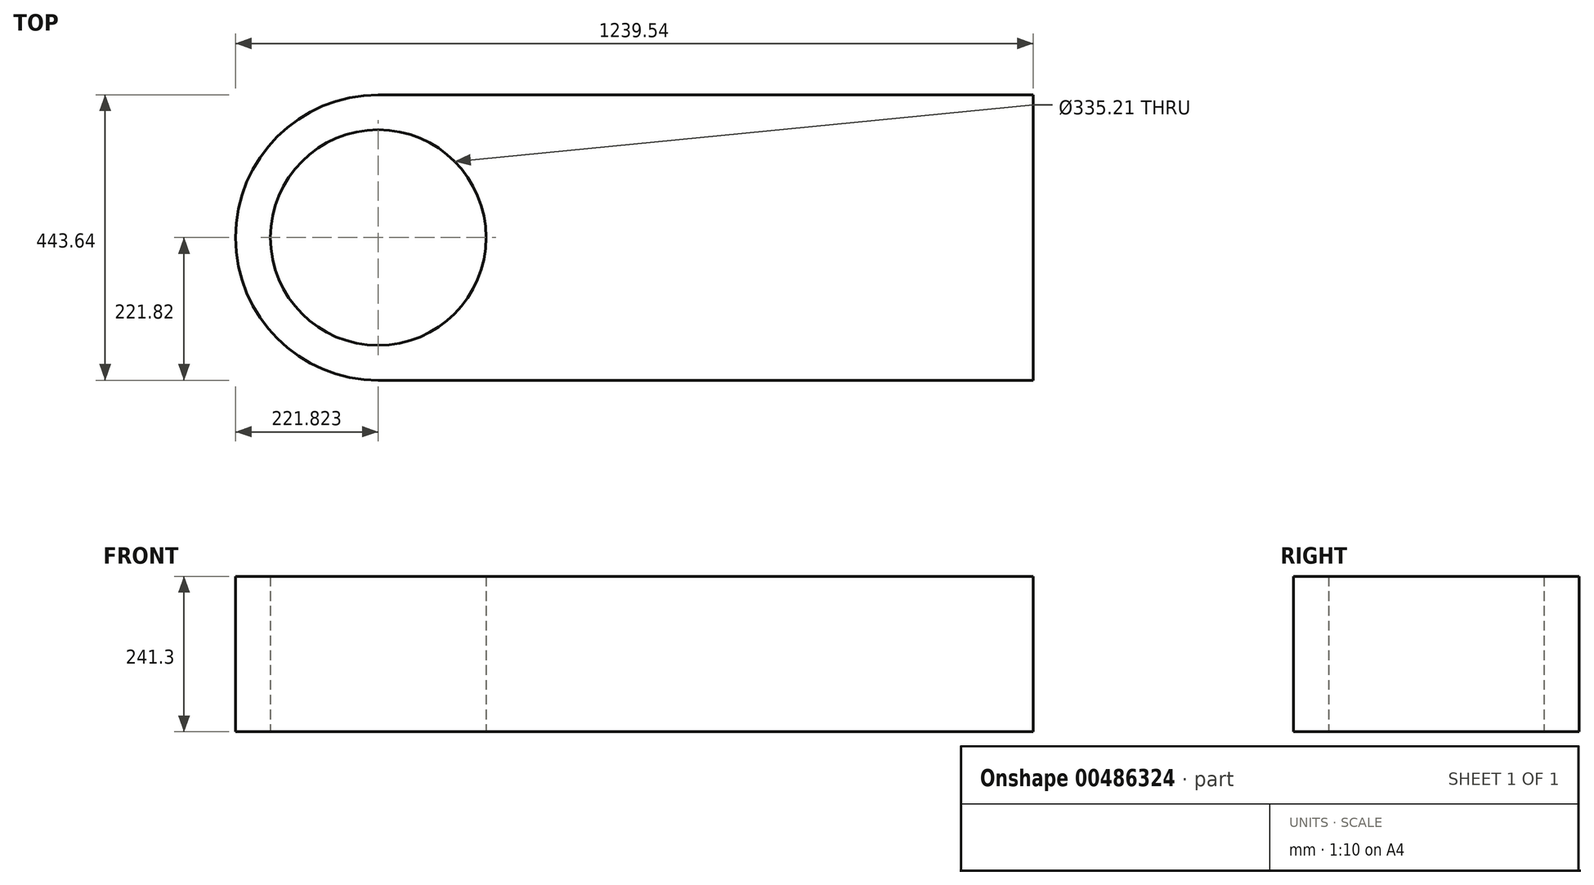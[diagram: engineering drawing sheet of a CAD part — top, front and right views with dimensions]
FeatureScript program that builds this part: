
annotation { "Feature Type Name" : "Feature", "Feature Type Description" : "" }
export const myFeature = defineFeature(function(context is Context, id is Id, definition is map)
    precondition{}
    {
        {
            var Q0;
            Q0=qCreatedBy(makeId("Top.planeOp"),FACE);
            var sketch = newSketch(context, id + "F0", { "sketchPlane" : qUnion([Q0])});
            skLineSegment(sketch, "E0.bottom", {"start": v(-508.86, -221.82) * mm, "end": v(508.86, -221.82) * mm});
            skLineSegment(sketch, "E0.top", {"start": v(-508.86, 221.82) * mm, "end": v(508.86, 221.82) * mm});
            skLineSegment(sketch, "E0.left", {"start": v(-508.86, -221.82) * mm, "end": v(-508.86, 221.82) * mm});
            skLineSegment(sketch, "E0.right", {"start": v(508.86, -221.82) * mm, "end": v(508.86, 221.82) * mm});
            skPoint(sketch, "E0.middle", {"position": v(0, 0) * mm});
            skCircle(sketch, "E1", {"center": v(-508.86, 0) * mm, "radius": 221.82 * mm});
            skCircle(sketch, "E2", {"center": v(-508.86, 0) * mm, "radius": 167.6 * mm});
            skSolve(sketch);
        }
        {
            var Q0;
            Q0 = qSketchRegion(id + "F0", true);
            extrude(context, id + "F1", {"entities" : qUnion([Q0]), "depth" : 241.3 * mm});
        }
    });
